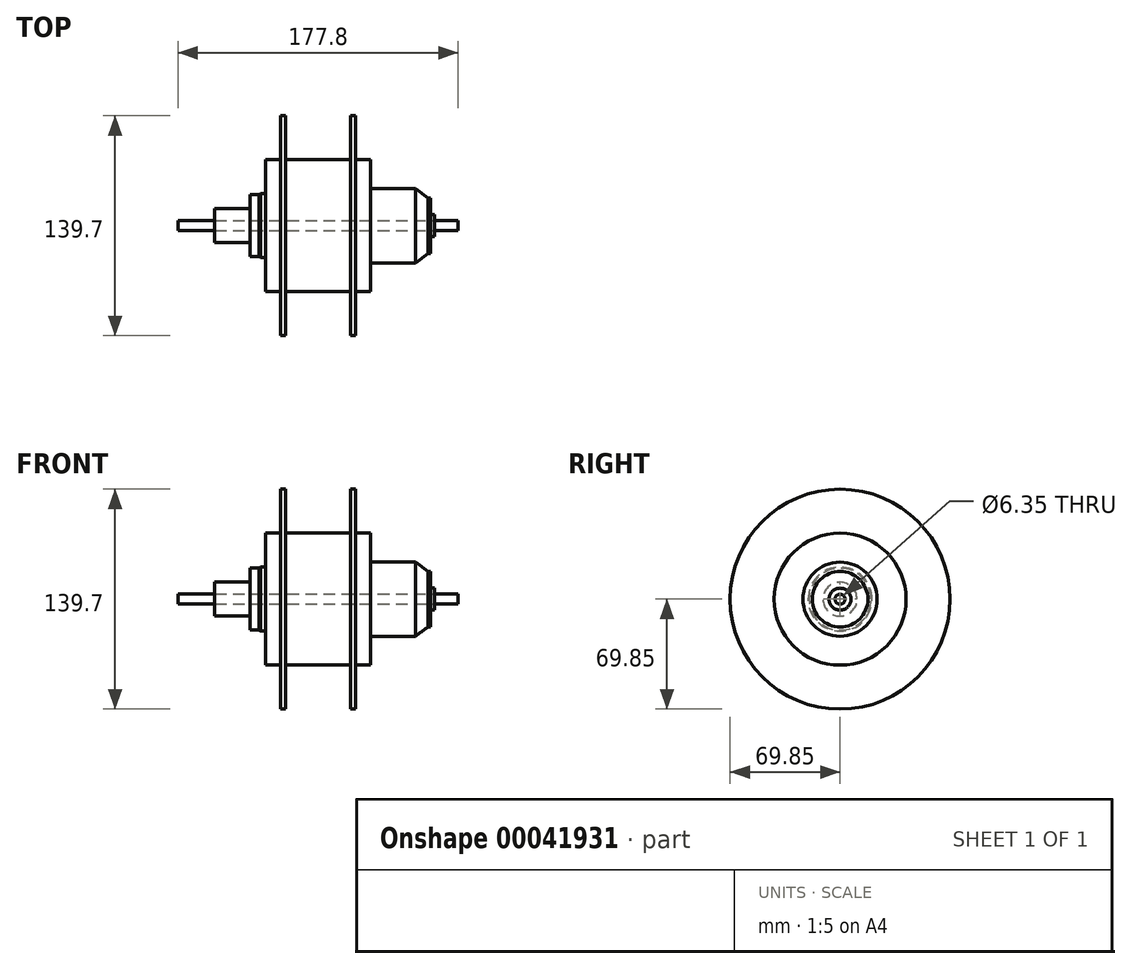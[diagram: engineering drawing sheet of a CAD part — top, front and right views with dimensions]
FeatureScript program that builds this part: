
annotation { "Feature Type Name" : "Feature", "Feature Type Description" : "" }
export const myFeature = defineFeature(function(context is Context, id is Id, definition is map)
    precondition{}
    {
        {
            var Q0;
            Q0=qCreatedBy(makeId("Right.planeOp"),FACE);
            var sketch = newSketch(context, id + "F0", { "sketchPlane" : qUnion([Q0])});
            skCircle(sketch, "E0", {"center": v(0, 0) * mm, "radius": 3.18 * mm});
            skSolve(sketch);
        }
        {
            var Q0;
            Q0=makeQuery(id+"F0.imprint","IMPRINT",FACE,{"disambiguationData":[TD([[makeQuery(id+"F0.imprint","IMPRINT",EDGE,{"derivedFrom":sQuery(id+"F0.wireOp",EDGE,"E0")}),1.0]])]});
            extrude(context, id + "F1", {"entities" : qUnion([Q0]), "endBound" : BoundingType.SYMMETRIC, "depth" : 177.8 * mm});
        }
        {
            var Q0;
            Q0=qCreatedBy(makeId("Front.planeOp"),FACE);
            var sketch = newSketch(context, id + "F2", { "sketchPlane" : qUnion([Q0])});
            skLineSegment(sketch, "E1", {"start": v(0, 0) * mm, "end": v(0, 41.9) * mm, "construction": true});
            skLineSegment(sketch, "E2.0", {"start": v(-88.9, 3.18) * mm, "end": v(-88.9, -3.18) * mm});
            skLineSegment(sketch, "E2.1", {"start": v(88.9, 3.18) * mm, "end": v(88.9, -3.18) * mm});
            skLineSegment(sketch, "E3", {"start": v(-65.57, 3.18) * mm, "end": v(74.13, 3.18) * mm});
            skLineSegment(sketch, "E4", {"start": v(74.13, 3.18) * mm, "end": v(74.13, 6.99) * mm});
            skLineSegment(sketch, "E5", {"start": v(74.13, 6.99) * mm, "end": v(71.55, 6.99) * mm});
            skLineSegment(sketch, "E6", {"start": v(71.55, 6.99) * mm, "end": v(71.55, 17.65) * mm});
            skLineSegment(sketch, "E7", {"start": v(71.55, 17.65) * mm, "end": v(69.83, 17.65) * mm});
            skLineSegment(sketch, "E8", {"start": v(69.83, 17.65) * mm, "end": v(61.84, 23.56) * mm});
            skLineSegment(sketch, "E9", {"start": v(61.84, 23.56) * mm, "end": v(33.2, 23.56) * mm});
            skLineSegment(sketch, "E10", {"start": v(33.2, 23.56) * mm, "end": v(33.2, 41.9) * mm});
            skLineSegment(sketch, "E11", {"start": v(33.2, 41.91) * mm, "end": v(23.92, 41.9) * mm});
            skLineSegment(sketch, "E12", {"start": v(23.92, 41.9) * mm, "end": v(23.92, 69.85) * mm});
            skLineSegment(sketch, "E13", {"start": v(23.92, 69.85) * mm, "end": v(20.62, 69.85) * mm});
            skLineSegment(sketch, "E14", {"start": v(20.62, 69.85) * mm, "end": v(20.62, 41.9) * mm});
            skLineSegment(sketch, "E15", {"start": v(20.62, 41.9) * mm, "end": v(-20.62, 41.9) * mm});
            skLineSegment(sketch, "E16", {"start": v(-20.62, 41.9) * mm, "end": v(-20.62, 69.85) * mm});
            skLineSegment(sketch, "E17", {"start": v(-20.62, 69.85) * mm, "end": v(-23.92, 69.85) * mm});
            skLineSegment(sketch, "E18", {"start": v(-23.92, 69.85) * mm, "end": v(-23.92, 41.9) * mm});
            skLineSegment(sketch, "E19", {"start": v(-23.92, 41.9) * mm, "end": v(-33.2, 41.9) * mm});
            skLineSegment(sketch, "E20", {"start": v(-33.2, 41.9) * mm, "end": v(-33.2, 20.32) * mm});
            skLineSegment(sketch, "E21", {"start": v(-33.2, 20.32) * mm, "end": v(-36.42, 20.32) * mm});
            skLineSegment(sketch, "E22", {"start": v(-36.42, 20.32) * mm, "end": v(-37.5, 19.68) * mm});
            skLineSegment(sketch, "E23", {"start": v(-37.5, 19.69) * mm, "end": v(-43.03, 19.69) * mm});
            skLineSegment(sketch, "E24", {"start": v(-43.03, 19.69) * mm, "end": v(-43.03, 10.79) * mm});
            skLineSegment(sketch, "E25", {"start": v(-43.03, 10.79) * mm, "end": v(-65.57, 10.79) * mm});
            skLineSegment(sketch, "E26", {"start": v(-65.57, 10.79) * mm, "end": v(-65.57, 3.18) * mm});
            skLineSegment(sketch, "E27", {"start": v(0, 0) * mm, "end": v(108.81, 0) * mm, "construction": true});
            skSolve(sketch);
        }
        {
            var Q0;
            Q0=makeQuery(id+"F2.imprint","IMPRINT",FACE,{"disambiguationData":[TD([[makeQuery(id+"F2.imprint","IMPRINT",EDGE,{"derivedFrom":sQuery(id+"F2.wireOp",EDGE,"E3")}),1.0]])]});
            var Q1;
            Q1=makeQuery(id+"F1.opExtrude","SWEPT_FACE",FACE,{"disambiguationData":[OSD([sQuery(id+"F0.wireOp",EDGE,"E0")])]});
            revolve(context, id + "F3", {"entities" : qUnion([Q0]), "axis" : qUnion([Q1]), "revolveType" : RevolveType.FULL});
        }
    });
